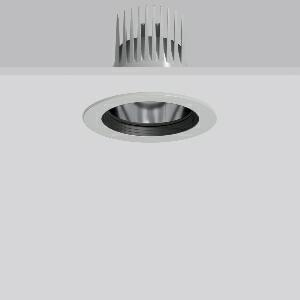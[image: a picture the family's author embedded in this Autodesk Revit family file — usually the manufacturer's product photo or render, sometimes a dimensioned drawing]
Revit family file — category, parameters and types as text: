
# Revit family: heledon_maxi_e_901779_004_76_96ad
name_source: partatom
category: Lighting Fixtures
units: mm (PartAtom-declared; Revit-internal decimal feet)

## family parameters
Cut with Voids When Loaded = No
Host = Face
Light Source = No
Part Type = Normal
Room Calculation Point = No
Round Connector Dimension = Use Diameter
Shared = No

## types (1)
- HELEDON maxi E (1 x LED Modul 920 meat+, 2250 lm, 2000)
    Apparent Load = 33 VA
    Approval mark = CE
    CIE Flux Codes = 100 100 100 100 100
    Color Rendering = 90
    Color Temperature = 2000
    Default Elevation = 1800 mm
    Description = Series: HELEDON maxi
Round recessed downlight. Housing: die-cast aluminium, powder-coated. Black plastic ring and recessed LED to prevent glare from the side. Optical assembly with reflector made of MIRO-Silver with 98% total light reflection for outstanding efficiency - can be changed without tools. Special LED for illumination of meat included. Suitable for Recessed ceiling mounting. Installation without tools thanks to spring fastening system. Including separate LED converter with connecting cable 600 mm.High quality converter without flickering and stroboscopic effect. Through-wiring box (5 pole) available as accessory. The following accessories can be mounted without use of tools: interchangeable lenses, decorative glasses, honeycomb louvre, clear and frosted diffusers, white interchangeable plastic ring. 
Colour: silver
Diameter: 162 mm
Height: 3 mm
Cut-out diameter: 152 mm
Recess height: 200 mm
Luminaire: recess height: 135 mm
Lamp: LED
Socket: without socket
Colour temperature: meat +
System power: 33 W
Rated luminous flux: 2250 lm
Luminous efficiency: 68 lm/W
Control gear: Converter, dimmable, DALI
Protection class: II
Type of protection: IP 20
    Height = 0 mm  [stored 0 ft]
    Lamp = 1 x LED Modul 920 meat+
    Lamp Light Flux = 2250 lm
    Lamp count = 1
    Length = 162 mm
    Lifetime = 50000 h
    Luminous efficacy = 68 lm/W
    Manufacturer = RZB
    ModVariant = No
    Model = 901779.004.76
    Mounting Place = Ceiling
    Mounting Type = Recessed
    Number of Poles = 1
    OnlyDefault = Yes
    Power Factor = 1
    Product Name = HELEDON maxi E
    Product group = Recessed downlights
    ProductGroupID = 402
    Protection Class = Protection class II
    Protection Degree = IP 20
    RLX_Detail_Level = 1
    RLX_Emergency_Light_Flux = 0 lm
    RLX_Emergency_Type = 0
    RLX_Emergency_Type_DB = No
    RlxData = <blob elided: 119165 chars, md5=5cca5de3>
    Socket = socket
    Standby Power = 0 W
    System Light Flux = 2250 lm
    System Power = 33 W
    Type Comments = Product without accessories
    Type Image = 901662.004.jpg
    URL = http://relux.com
    VarID = ---
    Voltage = 230 V
    Voltage Range = 220-240 V
    Weight = 0.00 kg
    Width = 0 mm  [stored 0 ft]

note: [stored X ft] marks values corroborated as IEEE doubles in the binary element streams (Revit-internal decimal feet)

## geometry (parser evidence)
native form markers: Blend x4, Sweep x9
no freeform markers — native parametric forms only
